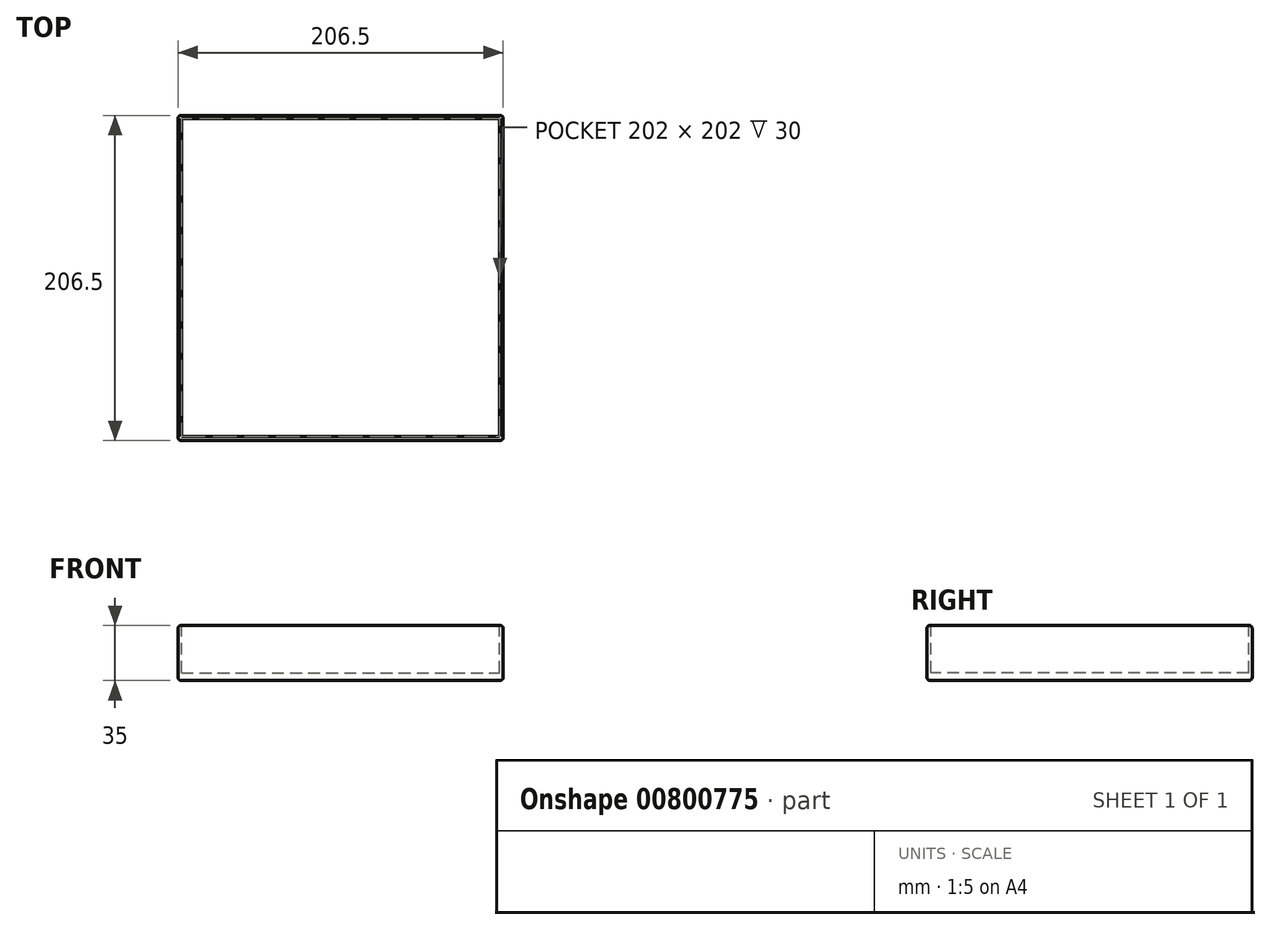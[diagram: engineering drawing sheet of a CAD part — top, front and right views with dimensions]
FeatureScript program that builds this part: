
annotation { "Feature Type Name" : "Feature", "Feature Type Description" : "" }
export const myFeature = defineFeature(function(context is Context, id is Id, definition is map)
    precondition{}
    {
        {
            var Q0;
            Q0=qCreatedBy(makeId("Top.planeOp"),FACE);
            var sketch = newSketch(context, id + "F0", { "sketchPlane" : qUnion([Q0])});
            skLineSegment(sketch, "E0.bottom", {"start": v(-133.74, 103.42) * mm, "end": v(72.76, 103.42) * mm});
            skLineSegment(sketch, "E0.top", {"start": v(-133.74, -103.08) * mm, "end": v(72.76, -103.08) * mm});
            skLineSegment(sketch, "E0.left", {"start": v(-133.74, 103.42) * mm, "end": v(-133.74, -103.08) * mm});
            skLineSegment(sketch, "E0.right", {"start": v(72.76, 103.42) * mm, "end": v(72.76, -103.08) * mm});
            skSolve(sketch);
        }
        {
            var Q0;
            Q0 = qSketchRegion(id + "F0", true);
            extrude(context, id + "F1", {"entities" : qUnion([Q0]), "depth" : 35 * mm, "offsetDistance" : 25 * mm});
        }
        {
            var Q0;
            Q0=makeQuery(id+"F1.opExtrude","CAP_FACE",FACE,{"disambiguationData":[OSD([sQuery(id+"F0.wireOp",EDGE,"E0.bottom"),sQuery(id+"F0.wireOp",EDGE,"E0.top"),sQuery(id+"F0.wireOp",EDGE,"E0.left"),sQuery(id+"F0.wireOp",EDGE,"E0.right")])],"isStart":false});
            var sketch = newSketch(context, id + "F2", { "sketchPlane" : qUnion([Q0])});
            skLineSegment(sketch, "E1.bottom", {"start": v(-131.59, 101.3) * mm, "end": v(70.41, 101.3) * mm});
            skLineSegment(sketch, "E1.top", {"start": v(-131.59, -100.7) * mm, "end": v(70.41, -100.7) * mm});
            skLineSegment(sketch, "E1.left", {"start": v(-131.59, 101.3) * mm, "end": v(-131.59, -100.7) * mm});
            skLineSegment(sketch, "E1.right", {"start": v(70.41, 101.3) * mm, "end": v(70.41, -100.7) * mm});
            skSolve(sketch);
        }
        {
            var Q0;
            Q0 = qSketchRegion(id + "F2", true);
            extrude(context, id + "F3", {"entities" : qUnion([Q0]), "operationType" : NewBodyOperationType.REMOVE, "oppositeDirection" : true, "depth" : 30 * mm, "offsetDistance" : 25 * mm});
        }
        {
            var Q0;
            Q0=makeQuery(id+"F1.opExtrude","SWEPT_FACE",FACE,{"disambiguationData":[OSD([sQuery(id+"F0.wireOp",EDGE,"E0.top")])]});
            var Q1;
            Q1=makeQuery(id+"F1.opExtrude","CAP_FACE",FACE,{"disambiguationData":[OSD([sQuery(id+"F0.wireOp",EDGE,"E0.bottom"),sQuery(id+"F0.wireOp",EDGE,"E0.top"),sQuery(id+"F0.wireOp",EDGE,"E0.left"),sQuery(id+"F0.wireOp",EDGE,"E0.right")])],"isStart":true});
            var Q2;
            Q2=makeQuery(id+"F1.opExtrude","SWEPT_FACE",FACE,{"disambiguationData":[OSD([sQuery(id+"F0.wireOp",EDGE,"E0.left")])]});
            var Q3;
            Q3=makeQuery(id+"F1.opExtrude","SWEPT_FACE",FACE,{"disambiguationData":[OSD([sQuery(id+"F0.wireOp",EDGE,"E0.bottom")])]});
            var Q4;
            Q4=makeQuery(id+"F1.opExtrude","SWEPT_FACE",FACE,{"disambiguationData":[OSD([sQuery(id+"F0.wireOp",EDGE,"E0.right")])]});
            fillet(context, id + "F4", {"entities" : qUnion([Q0, Q1, Q2, Q3, Q4]), "radius" : 2 * mm, "tangentPropagation" : true, "allowEdgeOverflow" : false});
        }
    });
